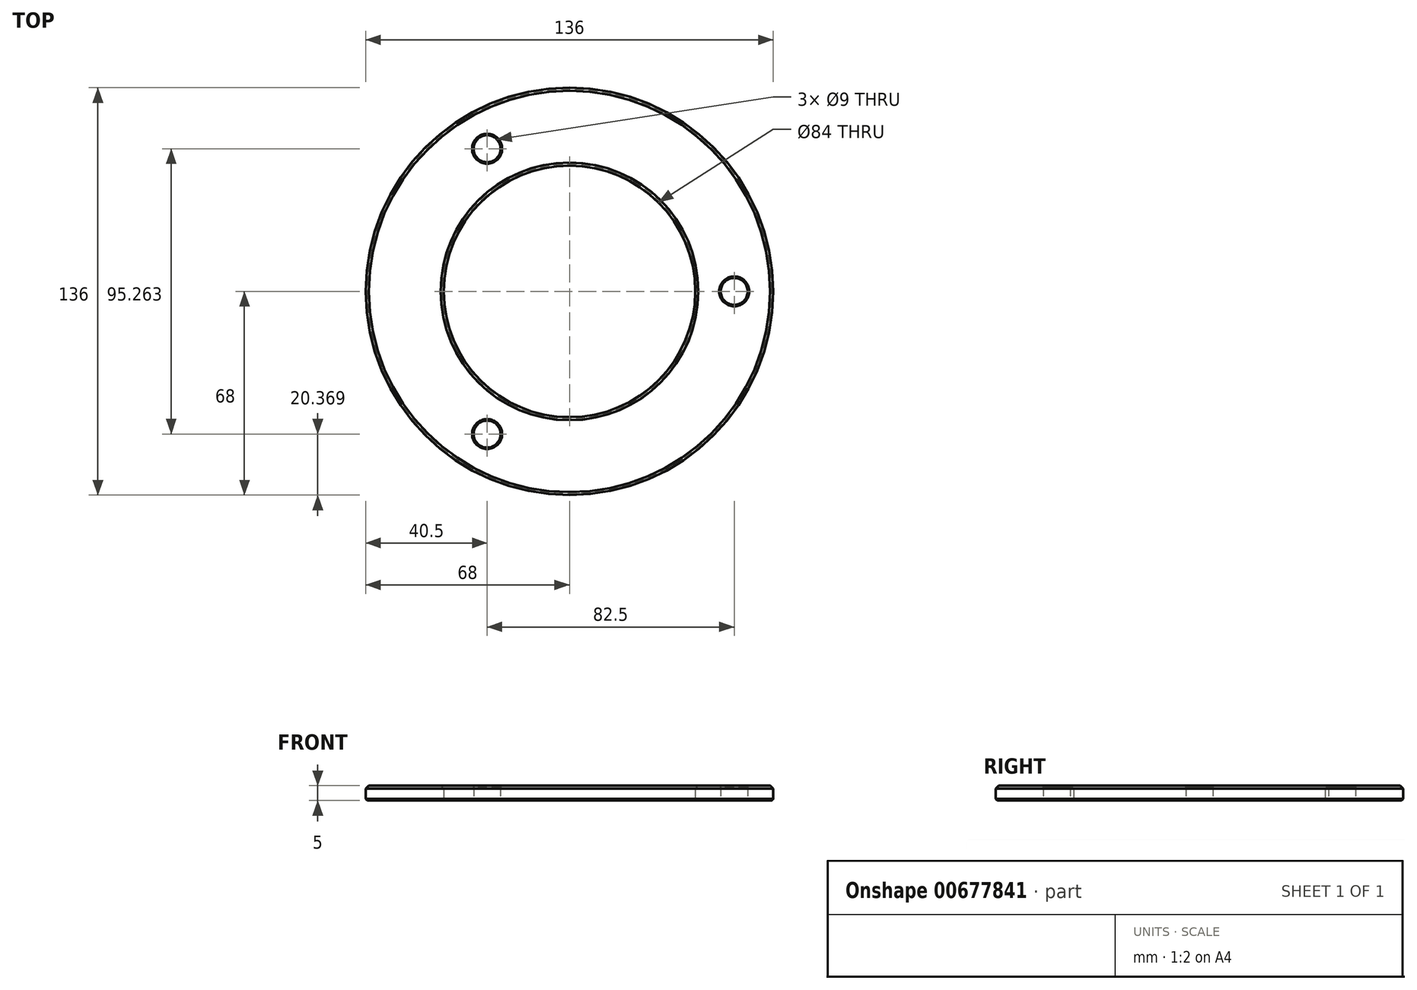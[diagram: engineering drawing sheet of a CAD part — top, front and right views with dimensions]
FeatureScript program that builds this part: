
annotation { "Feature Type Name" : "Feature", "Feature Type Description" : "" }
export const myFeature = defineFeature(function(context is Context, id is Id, definition is map)
    precondition{}
    {
        {
            var Q0;
            Q0=qCreatedBy(makeId("Top.planeOp"),FACE);
            var sketch = newSketch(context, id + "F0", { "sketchPlane" : qUnion([Q0])});
            skLineSegment(sketch, "E0", {"start": v(0, 98.73) * mm, "end": v(0, -162.18) * mm, "construction": true});
            skLineSegment(sketch, "E1", {"start": v(-170.8, 0) * mm, "end": v(192.12, 0) * mm, "construction": true});
            skCircle(sketch, "E2", {"center": v(0, 0) * mm, "radius": 55 * mm, "construction": true});
            skCircle(sketch, "E3", {"center": v(0, 0) * mm, "radius": 68 * mm});
            skCircle(sketch, "E4", {"center": v(0, 0) * mm, "radius": 42 * mm});
            skCircle(sketch, "E5", {"center": v(55, 0) * mm, "radius": 4.5 * mm});
            skCircle(sketch, "E6.1.0", {"center": v(-27.5, 47.63) * mm, "radius": 4.5 * mm});
            skCircle(sketch, "E6.2.0", {"center": v(-27.5, -47.63) * mm, "radius": 4.5 * mm});
            skLineSegment(sketch, "E7", {"start": v(66.93, 12) * mm, "end": v(-66.93, 12) * mm});
            skLineSegment(sketch, "E8", {"start": v(-65.84, 17) * mm, "end": v(65.84, 17) * mm});
            skPoint(sketch, "E9.orphan", {"position": v(91.12, 12) * mm});
            skLineSegment(sketch, "E10", {"start": v(-57.05, 37) * mm, "end": v(57.05, 37) * mm});
            skLineSegment(sketch, "E11", {"start": v(-60, 32) * mm, "end": v(60, 32) * mm});
            skCircle(sketch, "E12", {"center": v(0, 0) * mm, "radius": 43 * mm});
            skPoint(sketch, "E13.endSnap0", {"position": v(0, 37) * mm});
            skCircle(sketch, "E14", {"center": v(0, 0) * mm, "radius": 67 * mm});
            skSolve(sketch);
        }
        {
            var Q0;
            {var subQ0=sQuery(id+"F0.wireOp",EDGE,"E10");var subQ1=sQuery(id+"F0.wireOp",EDGE,"E3");var subQ2=makeQuery(id+"F0.imprint","INTERSECT",VERTEX,{"disambiguationData":[OD(0.0)],"derivedFrom":[subQ1,subQ0]});Q0=makeQuery(id+"F0.imprint","IMPRINT",FACE,{"disambiguationData":[TD([[makeQuery(id+"F0.imprint","IMPRINT",EDGE,{"disambiguationData":[TD([[subQ2,1.0]])],"derivedFrom":subQ1}),1.0]])]});}
            var Q1;
            Q1=makeQuery(id+"F0.imprint","IMPRINT",FACE,{"disambiguationData":[TD([[makeQuery(id+"F0.imprint","IMPRINT",EDGE,{"derivedFrom":sQuery(id+"F0.wireOp",EDGE,"E6.1.0")}),-1.0]])]});
            var Q2;
            {var subQ0=sQuery(id+"F0.wireOp",EDGE,"E10");var subQ1=sQuery(id+"F0.wireOp",EDGE,"E4");var subQ2=makeQuery(id+"F0.imprint","INTERSECT",VERTEX,{"disambiguationData":[OD(0.0)],"derivedFrom":[subQ1,subQ0]});Q2=makeQuery(id+"F0.imprint","IMPRINT",FACE,{"disambiguationData":[TD([[makeQuery(id+"F0.imprint","IMPRINT",EDGE,{"disambiguationData":[TD([[subQ2,-1.0]])],"derivedFrom":subQ1}),-1.0]])]});}
            var Q3;
            {var subQ0=sQuery(id+"F0.wireOp",EDGE,"E10");var subQ1=sQuery(id+"F0.wireOp",EDGE,"E4");var subQ2=makeQuery(id+"F0.imprint","INTERSECT",VERTEX,{"disambiguationData":[OD(1.0)],"derivedFrom":[subQ1,subQ0]});Q3=makeQuery(id+"F0.imprint","IMPRINT",FACE,{"disambiguationData":[TD([[makeQuery(id+"F0.imprint","IMPRINT",EDGE,{"disambiguationData":[TD([[subQ2,-1.0]])],"derivedFrom":subQ1}),-1.0]])]});}
            var Q4;
            {var subQ0=sQuery(id+"F0.wireOp",EDGE,"E14");var subQ1=sQuery(id+"F0.wireOp",EDGE,"E10");var subQ2=makeQuery(id+"F0.imprint","INTERSECT",VERTEX,{"disambiguationData":[OD(0.0)],"derivedFrom":[subQ1,subQ0]});Q4=makeQuery(id+"F0.imprint","IMPRINT",FACE,{"disambiguationData":[TD([[makeQuery(id+"F0.imprint","IMPRINT",EDGE,{"disambiguationData":[TD([[subQ2,-1.0]])],"derivedFrom":subQ1}),-1.0]])]});}
            var Q5;
            {var subQ0=sQuery(id+"F0.wireOp",EDGE,"E10");var subQ1=sQuery(id+"F0.wireOp",EDGE,"E3");var subQ2=makeQuery(id+"F0.imprint","INTERSECT",VERTEX,{"disambiguationData":[OD(0.0)],"derivedFrom":[subQ1,subQ0]});Q5=makeQuery(id+"F0.imprint","IMPRINT",FACE,{"disambiguationData":[TD([[makeQuery(id+"F0.imprint","IMPRINT",EDGE,{"disambiguationData":[TD([[subQ2,-1.0]])],"derivedFrom":subQ1}),1.0]])]});}
            var Q6;
            {var subQ0=sQuery(id+"F0.wireOp",EDGE,"E14");var subQ1=sQuery(id+"F0.wireOp",EDGE,"E8");var subQ2=makeQuery(id+"F0.imprint","INTERSECT",VERTEX,{"disambiguationData":[OD(0.0)],"derivedFrom":[subQ1,subQ0]});Q6=makeQuery(id+"F0.imprint","IMPRINT",FACE,{"disambiguationData":[TD([[makeQuery(id+"F0.imprint","IMPRINT",EDGE,{"disambiguationData":[TD([[subQ2,-1.0]])],"derivedFrom":subQ1}),1.0]])]});}
            var Q7;
            {var subQ0=sQuery(id+"F0.wireOp",EDGE,"E8");var subQ1=sQuery(id+"F0.wireOp",EDGE,"E3");var subQ2=makeQuery(id+"F0.imprint","INTERSECT",VERTEX,{"disambiguationData":[OD(0.0)],"derivedFrom":[subQ1,subQ0]});Q7=makeQuery(id+"F0.imprint","IMPRINT",FACE,{"disambiguationData":[TD([[makeQuery(id+"F0.imprint","IMPRINT",EDGE,{"disambiguationData":[TD([[subQ2,1.0]])],"derivedFrom":subQ1}),1.0]])]});}
            var Q8;
            {var subQ0=sQuery(id+"F0.wireOp",EDGE,"E11");var subQ1=sQuery(id+"F0.wireOp",EDGE,"E4");var subQ2=makeQuery(id+"F0.imprint","INTERSECT",VERTEX,{"disambiguationData":[OD(1.0)],"derivedFrom":[subQ1,subQ0]});Q8=makeQuery(id+"F0.imprint","IMPRINT",FACE,{"disambiguationData":[TD([[makeQuery(id+"F0.imprint","IMPRINT",EDGE,{"disambiguationData":[TD([[subQ2,-1.0]])],"derivedFrom":subQ1}),-1.0]])]});}
            var Q9;
            {var subQ0=sQuery(id+"F0.wireOp",EDGE,"E12");var subQ1=sQuery(id+"F0.wireOp",EDGE,"E8");var subQ2=makeQuery(id+"F0.imprint","INTERSECT",VERTEX,{"disambiguationData":[OD(1.0)],"derivedFrom":[subQ1,subQ0]});Q9=makeQuery(id+"F0.imprint","IMPRINT",FACE,{"disambiguationData":[TD([[makeQuery(id+"F0.imprint","IMPRINT",EDGE,{"disambiguationData":[TD([[subQ2,-1.0]])],"derivedFrom":subQ1}),1.0]])]});}
            var Q10;
            {var subQ0=sQuery(id+"F0.wireOp",EDGE,"E10");var subQ1=sQuery(id+"F0.wireOp",EDGE,"E3");var subQ2=makeQuery(id+"F0.imprint","INTERSECT",VERTEX,{"disambiguationData":[OD(1.0)],"derivedFrom":[subQ1,subQ0]});Q10=makeQuery(id+"F0.imprint","IMPRINT",FACE,{"disambiguationData":[TD([[makeQuery(id+"F0.imprint","IMPRINT",EDGE,{"disambiguationData":[TD([[subQ2,1.0]])],"derivedFrom":subQ1}),1.0]])]});}
            var Q11;
            {var subQ0=sQuery(id+"F0.wireOp",EDGE,"E12");var subQ1=sQuery(id+"F0.wireOp",EDGE,"E10");var subQ2=makeQuery(id+"F0.imprint","INTERSECT",VERTEX,{"disambiguationData":[OD(1.0)],"derivedFrom":[subQ1,subQ0]});Q11=makeQuery(id+"F0.imprint","IMPRINT",FACE,{"disambiguationData":[TD([[makeQuery(id+"F0.imprint","IMPRINT",EDGE,{"disambiguationData":[TD([[subQ2,-1.0]])],"derivedFrom":subQ1}),-1.0]])]});}
            var Q12;
            {var subQ0=sQuery(id+"F0.wireOp",EDGE,"E11");var subQ1=sQuery(id+"F0.wireOp",EDGE,"E4");var subQ2=makeQuery(id+"F0.imprint","INTERSECT",VERTEX,{"disambiguationData":[OD(0.0)],"derivedFrom":[subQ1,subQ0]});Q12=makeQuery(id+"F0.imprint","IMPRINT",FACE,{"disambiguationData":[TD([[makeQuery(id+"F0.imprint","IMPRINT",EDGE,{"disambiguationData":[TD([[subQ2,-1.0]])],"derivedFrom":subQ1}),-1.0]])]});}
            var Q13;
            {var subQ0=sQuery(id+"F0.wireOp",EDGE,"E8");var subQ1=sQuery(id+"F0.wireOp",EDGE,"E4");var subQ2=makeQuery(id+"F0.imprint","INTERSECT",VERTEX,{"disambiguationData":[OD(0.0)],"derivedFrom":[subQ1,subQ0]});Q13=makeQuery(id+"F0.imprint","IMPRINT",FACE,{"disambiguationData":[TD([[makeQuery(id+"F0.imprint","IMPRINT",EDGE,{"disambiguationData":[TD([[subQ2,-1.0]])],"derivedFrom":subQ1}),-1.0]])]});}
            var Q14;
            {var subQ0=sQuery(id+"F0.wireOp",EDGE,"E8");var subQ1=sQuery(id+"F0.wireOp",EDGE,"E3");var subQ2=makeQuery(id+"F0.imprint","INTERSECT",VERTEX,{"disambiguationData":[OD(1.0)],"derivedFrom":[subQ1,subQ0]});Q14=makeQuery(id+"F0.imprint","IMPRINT",FACE,{"disambiguationData":[TD([[makeQuery(id+"F0.imprint","IMPRINT",EDGE,{"disambiguationData":[TD([[subQ2,-1.0]])],"derivedFrom":subQ1}),1.0]])]});}
            var Q15;
            {var subQ0=sQuery(id+"F0.wireOp",EDGE,"E7");var subQ1=sQuery(id+"F0.wireOp",EDGE,"E3");var subQ2=makeQuery(id+"F0.imprint","INTERSECT",VERTEX,{"disambiguationData":[OD(0.0)],"derivedFrom":[subQ1,subQ0]});Q15=makeQuery(id+"F0.imprint","IMPRINT",FACE,{"disambiguationData":[TD([[makeQuery(id+"F0.imprint","IMPRINT",EDGE,{"disambiguationData":[TD([[subQ2,-1.0]])],"derivedFrom":subQ1}),1.0]])]});}
            var Q16;
            {var subQ0=sQuery(id+"F0.wireOp",EDGE,"E14");var subQ1=sQuery(id+"F0.wireOp",EDGE,"E7");var subQ2=makeQuery(id+"F0.imprint","INTERSECT",VERTEX,{"disambiguationData":[OD(0.0)],"derivedFrom":[subQ1,subQ0]});Q16=makeQuery(id+"F0.imprint","IMPRINT",FACE,{"disambiguationData":[TD([[makeQuery(id+"F0.imprint","IMPRINT",EDGE,{"disambiguationData":[TD([[subQ2,-1.0]])],"derivedFrom":subQ1}),-1.0]])]});}
            var Q17;
            {var subQ0=sQuery(id+"F0.wireOp",EDGE,"E8");var subQ1=sQuery(id+"F0.wireOp",EDGE,"E4");var subQ2=makeQuery(id+"F0.imprint","INTERSECT",VERTEX,{"disambiguationData":[OD(0.0)],"derivedFrom":[subQ1,subQ0]});Q17=makeQuery(id+"F0.imprint","IMPRINT",FACE,{"disambiguationData":[TD([[makeQuery(id+"F0.imprint","IMPRINT",EDGE,{"disambiguationData":[TD([[subQ2,1.0]])],"derivedFrom":subQ1}),-1.0]])]});}
            var Q18;
            {var subQ0=sQuery(id+"F0.wireOp",EDGE,"E7");var subQ1=sQuery(id+"F0.wireOp",EDGE,"E4");var subQ2=makeQuery(id+"F0.imprint","INTERSECT",VERTEX,{"disambiguationData":[OD(0.0)],"derivedFrom":[subQ1,subQ0]});Q18=makeQuery(id+"F0.imprint","IMPRINT",FACE,{"disambiguationData":[TD([[makeQuery(id+"F0.imprint","IMPRINT",EDGE,{"disambiguationData":[TD([[subQ2,1.0]])],"derivedFrom":subQ1}),-1.0]])]});}
            var Q19;
            Q19=makeQuery(id+"F0.imprint","IMPRINT",FACE,{"disambiguationData":[TD([[makeQuery(id+"F0.imprint","IMPRINT",EDGE,{"derivedFrom":sQuery(id+"F0.wireOp",EDGE,"E5")}),-1.0]])]});
            var Q20;
            {var subQ0=sQuery(id+"F0.wireOp",EDGE,"E7");var subQ1=sQuery(id+"F0.wireOp",EDGE,"E3");var subQ2=makeQuery(id+"F0.imprint","INTERSECT",VERTEX,{"disambiguationData":[OD(0.0)],"derivedFrom":[subQ1,subQ0]});Q20=makeQuery(id+"F0.imprint","IMPRINT",FACE,{"disambiguationData":[TD([[makeQuery(id+"F0.imprint","IMPRINT",EDGE,{"disambiguationData":[TD([[subQ2,1.0]])],"derivedFrom":subQ1}),1.0]])]});}
            var Q21;
            {var subQ0=sQuery(id+"F0.wireOp",EDGE,"E8");var subQ1=sQuery(id+"F0.wireOp",EDGE,"E4");var subQ2=makeQuery(id+"F0.imprint","INTERSECT",VERTEX,{"disambiguationData":[OD(1.0)],"derivedFrom":[subQ1,subQ0]});Q21=makeQuery(id+"F0.imprint","IMPRINT",FACE,{"disambiguationData":[TD([[makeQuery(id+"F0.imprint","IMPRINT",EDGE,{"disambiguationData":[TD([[subQ2,-1.0]])],"derivedFrom":subQ1}),-1.0]])]});}
            var Q22;
            {var subQ0=sQuery(id+"F0.wireOp",EDGE,"E7");var subQ1=sQuery(id+"F0.wireOp",EDGE,"E3");var subQ2=makeQuery(id+"F0.imprint","INTERSECT",VERTEX,{"disambiguationData":[OD(1.0)],"derivedFrom":[subQ1,subQ0]});Q22=makeQuery(id+"F0.imprint","IMPRINT",FACE,{"disambiguationData":[TD([[makeQuery(id+"F0.imprint","IMPRINT",EDGE,{"disambiguationData":[TD([[subQ2,1.0]])],"derivedFrom":subQ1}),1.0]])]});}
            var Q23;
            {var subQ0=sQuery(id+"F0.wireOp",EDGE,"E12");var subQ1=sQuery(id+"F0.wireOp",EDGE,"E7");var subQ2=makeQuery(id+"F0.imprint","INTERSECT",VERTEX,{"disambiguationData":[OD(1.0)],"derivedFrom":[subQ1,subQ0]});Q23=makeQuery(id+"F0.imprint","IMPRINT",FACE,{"disambiguationData":[TD([[makeQuery(id+"F0.imprint","IMPRINT",EDGE,{"disambiguationData":[TD([[subQ2,-1.0]])],"derivedFrom":subQ1}),-1.0]])]});}
            extrude(context, id + "F1", {"entities" : qUnion([Q0, Q1, Q2, Q3, Q4, Q5, Q6, Q7, Q8, Q9, Q10, Q11, Q12, Q13, Q14, Q15, Q16, Q17, Q18, Q19, Q20, Q21, Q22, Q23]), "depth" : 5 * mm, "offsetDistance" : 25 * mm});
        }
        {
            var Q0;
            Q0=makeQuery(id+"F1.opExtrude","CAP_EDGE",EDGE,{"disambiguationData":[OSD([sQuery(id+"F0.wireOp",EDGE,"E3")])],"isStart":false});
            var Q1;
            Q1=makeQuery(id+"F1.opExtrude","CAP_EDGE",EDGE,{"disambiguationData":[OSD([sQuery(id+"F0.wireOp",EDGE,"E4")])],"isStart":false});
            chamfer(context, id + "F2", {"entities" : qUnion([Q0, Q1]), "width" : 1 * mm, "tangentPropagation" : true});
        }
        {
            var Q0;
            Q0=makeQuery(id+"F1.opExtrude","CAP_EDGE",EDGE,{"disambiguationData":[OSD([sQuery(id+"F0.wireOp",EDGE,"E6.1.0")])],"isStart":false});
            var Q1;
            Q1=makeQuery(id+"F1.opExtrude","CAP_EDGE",EDGE,{"disambiguationData":[OSD([sQuery(id+"F0.wireOp",EDGE,"E4")])],"isStart":true});
            var Q2;
            Q2=makeQuery(id+"F1.opExtrude","CAP_EDGE",EDGE,{"disambiguationData":[OSD([sQuery(id+"F0.wireOp",EDGE,"E6.1.0")])],"isStart":true});
            var Q3;
            Q3=makeQuery(id+"F1.opExtrude","CAP_EDGE",EDGE,{"disambiguationData":[OSD([sQuery(id+"F0.wireOp",EDGE,"E3")])],"isStart":true});
            var Q4;
            Q4=makeQuery(id+"F1.opExtrude","CAP_EDGE",EDGE,{"disambiguationData":[OSD([sQuery(id+"F0.wireOp",EDGE,"E5")])],"isStart":false});
            var Q5;
            Q5=makeQuery(id+"F1.opExtrude","CAP_EDGE",EDGE,{"disambiguationData":[OSD([sQuery(id+"F0.wireOp",EDGE,"E5")])],"isStart":true});
            var Q6;
            Q6=makeQuery(id+"F1.opExtrude","CAP_EDGE",EDGE,{"disambiguationData":[OSD([sQuery(id+"F0.wireOp",EDGE,"E6.2.0")])],"isStart":false});
            var Q7;
            Q7=makeQuery(id+"F1.opExtrude","CAP_EDGE",EDGE,{"disambiguationData":[OSD([sQuery(id+"F0.wireOp",EDGE,"E6.2.0")])],"isStart":true});
            chamfer(context, id + "F3", {"entities" : qUnion([Q0, Q1, Q2, Q3, Q4, Q5, Q6, Q7]), "width" : 0.5 * mm, "tangentPropagation" : true});
        }
    });
